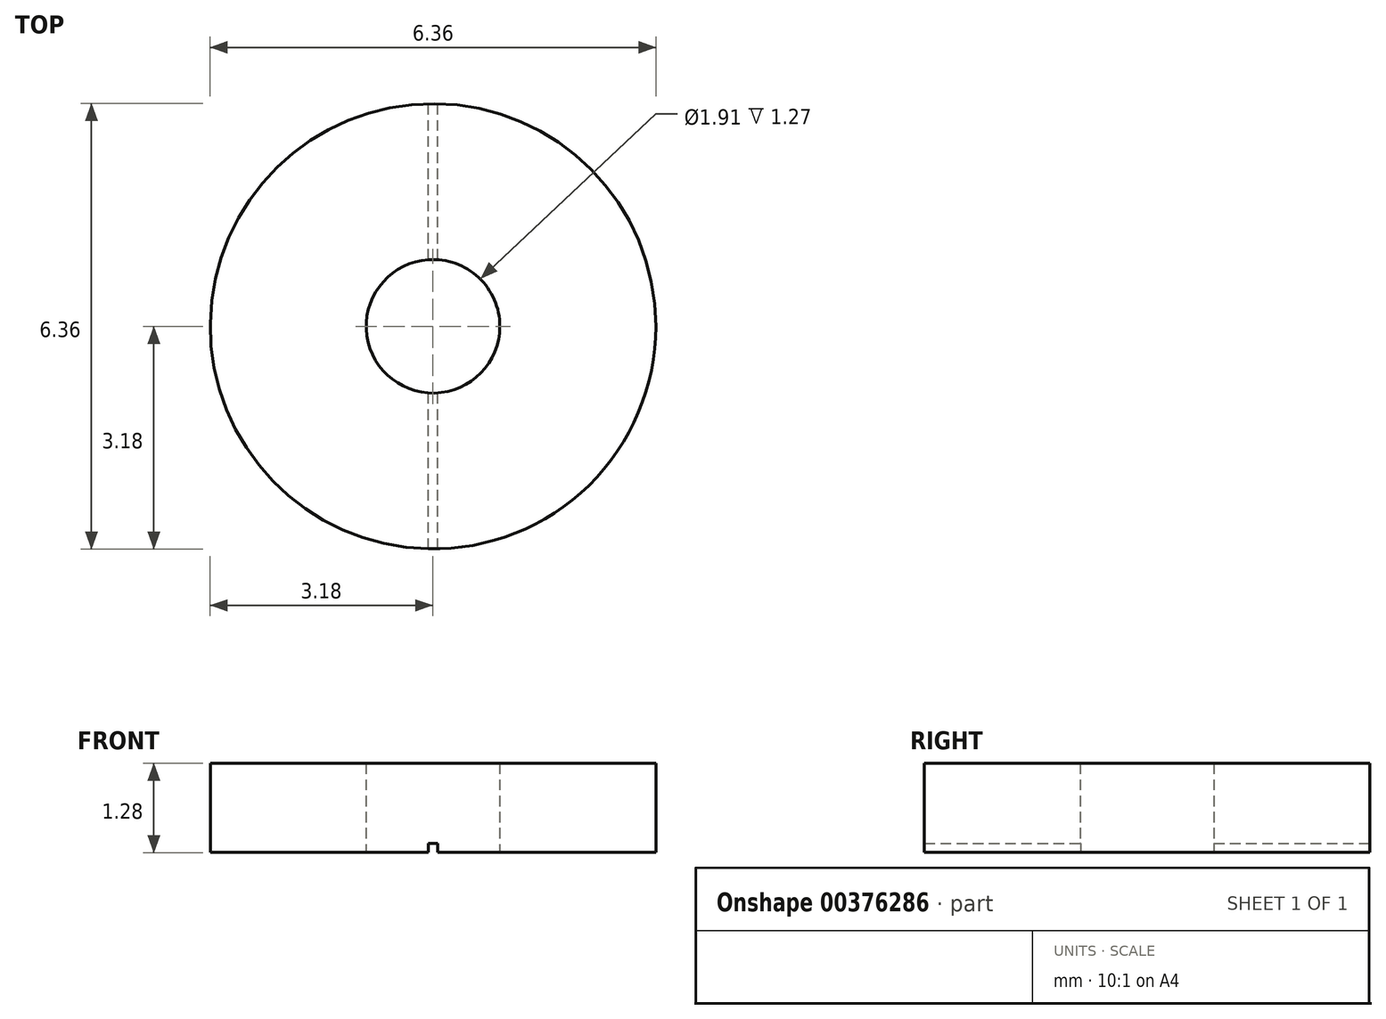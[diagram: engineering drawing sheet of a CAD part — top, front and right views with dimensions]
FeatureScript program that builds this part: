
annotation { "Feature Type Name" : "Feature", "Feature Type Description" : "" }
export const myFeature = defineFeature(function(context is Context, id is Id, definition is map)
    precondition{}
    {
        {
            var Q0;
            Q0=qCreatedBy(makeId("Top.planeOp"),FACE);
            var sketch = newSketch(context, id + "F0", { "sketchPlane" : qUnion([Q0])});
            skCircle(sketch, "E0", {"center": v(0, 0) * mm, "radius": 3.18 * mm});
            skCircle(sketch, "E1", {"center": v(0, 0) * mm, "radius": 0.95 * mm});
            skSolve(sketch);
        }
        {
            var Q0;
            Q0=makeQuery(id+"F0.imprint","IMPRINT",FACE,{"disambiguationData":[TD([[makeQuery(id+"F0.imprint","IMPRINT",EDGE,{"derivedFrom":sQuery(id+"F0.wireOp",EDGE,"E0")}),1.0]])]});
            extrude(context, id + "F1", {"entities" : qUnion([Q0]), "endBound" : BoundingType.SYMMETRIC, "depth" : 1.27 * mm});
        }
        {
            var Q0;
            Q0=makeQuery(id+"F1.opExtrude","CAP_FACE",FACE,{"disambiguationData":[OSD([sQuery(id+"F0.wireOp",EDGE,"E0"),sQuery(id+"F0.wireOp",EDGE,"E1")])],"isStart":true});
            var sketch = newSketch(context, id + "F2", { "sketchPlane" : qUnion([Q0])});
            skLineSegment(sketch, "E2.bottom", {"start": v(0.06, 3.81) * mm, "end": v(-0.06, 3.81) * mm});
            skLineSegment(sketch, "E2.top", {"start": v(0.06, -3.8) * mm, "end": v(-0.06, -3.8) * mm});
            skLineSegment(sketch, "E2.left", {"start": v(0.06, 3.81) * mm, "end": v(0.06, -3.8) * mm});
            skLineSegment(sketch, "E2.right", {"start": v(-0.06, 3.81) * mm, "end": v(-0.06, -3.8) * mm});
            skPoint(sketch, "E2.middle", {"position": v(0, 0) * mm});
            skSolve(sketch);
        }
        {
            var Q0;
            {var subQ0=sQuery(id+"F2.wireOp",EDGE,"E2.left");var subQ1=makeQuery(id+"F1.opExtrude","CAP_EDGE",EDGE,{"disambiguationData":[OSD([sQuery(id+"F0.wireOp",EDGE,"E0")])],"isStart":true});var subQ2=makeQuery(id+"F2.imprint","INTERSECT",VERTEX,{"disambiguationData":[OD(0.0)],"derivedFrom":[subQ1,subQ0]});Q0=makeQuery(id+"F2.imprint","IMPRINT",FACE,{"disambiguationData":[TD([[makeQuery(id+"F2.imprint","IMPRINT",EDGE,{"disambiguationData":[TD([[subQ2,-1.0]])],"derivedFrom":subQ0}),-1.0]])]});}
            var Q1;
            {var subQ0=sQuery(id+"F2.wireOp",EDGE,"E2.left");var subQ1=makeQuery(id+"F1.opExtrude","CAP_EDGE",EDGE,{"disambiguationData":[OSD([sQuery(id+"F0.wireOp",EDGE,"E0")])],"isStart":true});var subQ2=makeQuery(id+"F2.imprint","INTERSECT",VERTEX,{"disambiguationData":[OD(1.0)],"derivedFrom":[subQ1,subQ0]});Q1=makeQuery(id+"F2.imprint","IMPRINT",FACE,{"disambiguationData":[TD([[makeQuery(id+"F2.imprint","IMPRINT",EDGE,{"disambiguationData":[TD([[subQ2,1.0]])],"derivedFrom":subQ0}),-1.0]])]});}
            var Q2;
            {var subQ0=sQuery(id+"F2.wireOp",EDGE,"E2.top");Q2=makeQuery(id+"F2.imprint","IMPRINT",FACE,{"disambiguationData":[TD([[makeQuery(id+"F2.imprint","IMPRINT",EDGE,{"derivedFrom":subQ0}),-1.0]])]});}
            var Q3;
            {var subQ0=sQuery(id+"F2.wireOp",EDGE,"E2.left");var subQ1=makeQuery(id+"F1.opExtrude","CAP_EDGE",EDGE,{"disambiguationData":[OSD([sQuery(id+"F0.wireOp",EDGE,"E1")])],"isStart":true});var subQ2=makeQuery(id+"F2.imprint","INTERSECT",VERTEX,{"disambiguationData":[OD(0.0)],"derivedFrom":[subQ1,subQ0]});Q3=makeQuery(id+"F2.imprint","IMPRINT",FACE,{"disambiguationData":[TD([[makeQuery(id+"F2.imprint","IMPRINT",EDGE,{"disambiguationData":[TD([[subQ2,-1.0]])],"derivedFrom":subQ0}),-1.0]])]});}
            var Q4;
            {var subQ0=sQuery(id+"F2.wireOp",EDGE,"E2.bottom");Q4=makeQuery(id+"F2.imprint","IMPRINT",FACE,{"disambiguationData":[TD([[makeQuery(id+"F2.imprint","IMPRINT",EDGE,{"derivedFrom":subQ0}),1.0]])]});}
            extrude(context, id + "F3", {"entities" : qUnion([Q0, Q1, Q2, Q3, Q4]), "operationType" : NewBodyOperationType.REMOVE, "oppositeDirection" : true, "depth" : 0.13 * mm});
        }
    });
